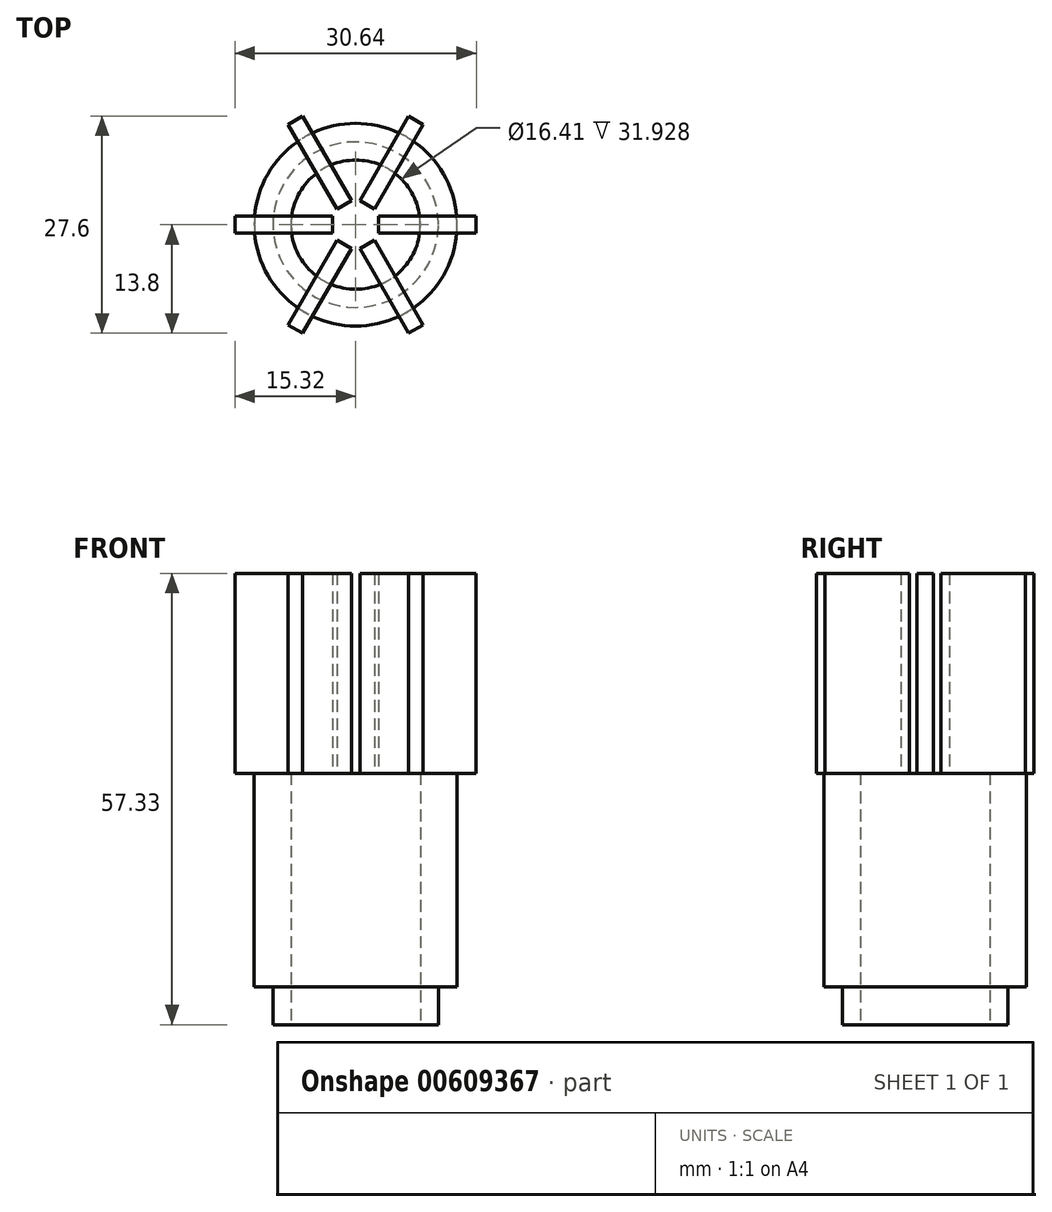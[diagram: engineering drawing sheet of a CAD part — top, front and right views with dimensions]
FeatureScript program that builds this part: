
annotation { "Feature Type Name" : "Feature", "Feature Type Description" : "" }
export const myFeature = defineFeature(function(context is Context, id is Id, definition is map)
    precondition{}
    {
        {
            var Q0;
            Q0=qCreatedBy(makeId("Front.planeOp"),FACE);
            var sketch = newSketch(context, id + "F0", { "sketchPlane" : qUnion([Q0])});
            skLineSegment(sketch, "E0", {"start": v(0, 0) * mm, "end": v(0, 36.56) * mm});
            skSolve(sketch);
        }
        {
            var Q0;
            Q0=qCreatedBy(makeId("Front.planeOp"),FACE);
            var sketch = newSketch(context, id + "F1", { "sketchPlane" : qUnion([Q0])});
            skLineSegment(sketch, "E1", {"start": v(8.2, 0) * mm, "end": v(12.88, 0) * mm});
            skLineSegment(sketch, "E2", {"start": v(12.88, 0) * mm, "end": v(12.88, -1.71) * mm});
            skLineSegment(sketch, "E3", {"start": v(12.88, -1.71) * mm, "end": v(10.5, -1.71) * mm});
            skLineSegment(sketch, "E4", {"start": v(10.5, -1.71) * mm, "end": v(10.5, -6.53) * mm});
            skLineSegment(sketch, "E5", {"start": v(10.5, -6.53) * mm, "end": v(8.2, -6.53) * mm});
            skLineSegment(sketch, "E6", {"start": v(8.2, -6.53) * mm, "end": v(8.2, 0) * mm});
            skSolve(sketch);
        }
        {
            var Q0;
            Q0=makeQuery(id+"F1.imprint","IMPRINT",FACE,{"disambiguationData":[TD([[makeQuery(id+"F1.imprint","IMPRINT",EDGE,{"derivedFrom":sQuery(id+"F1.wireOp",EDGE,"E1")}),-1.0]])]});
            var Q1;
            Q1=sQuery(id+"F0.wireOp",EDGE,"E0");
            revolve(context, id + "F2", {"entities" : qUnion([Q0]), "axis" : qUnion([Q1]), "revolveType" : RevolveType.FULL});
        }
        {
            var Q0;
            Q0=makeQuery(id+"F2.opRevolve","SWEPT_FACE",FACE,{"disambiguationData":[OSD([sQuery(id+"F1.wireOp",EDGE,"E1")])]});
            extrude(context, id + "F3", {"entities" : qUnion([Q0]), "operationType" : NewBodyOperationType.ADD, "depth" : 25.4 * mm, "offsetDistance" : 25.4 * mm});
        }
        {
            var Q0;
            Q0=makeQuery(id+"F3.opExtrude","CAP_FACE",FACE,{"disambiguationData":[OSD([sQuery(id+"F1.wireOp",EDGE,"E1")])],"isStart":false});
            var sketch = newSketch(context, id + "F4", { "sketchPlane" : qUnion([Q0])});
            skLineSegment(sketch, "E7.bottom", {"start": v(2.9, 1.07) * mm, "end": v(15.32, 1.07) * mm});
            skLineSegment(sketch, "E7.top", {"start": v(2.9, -1.07) * mm, "end": v(15.32, -1.07) * mm});
            skLineSegment(sketch, "E7.left", {"start": v(2.9, 1.07) * mm, "end": v(2.9, -1.07) * mm});
            skLineSegment(sketch, "E7.right", {"start": v(15.32, 1.07) * mm, "end": v(15.32, -1.07) * mm});
            skPoint(sketch, "E8", {"position": v(2.9, 0) * mm});
            skPoint(sketch, "E9.1.0", {"position": v(1.45, 2.52) * mm});
            skLineSegment(sketch, "E9.1.1", {"start": v(0.53, 3.05) * mm, "end": v(6.73, 13.8) * mm});
            skLineSegment(sketch, "E9.1.2", {"start": v(2.38, 1.99) * mm, "end": v(8.58, 12.73) * mm});
            skLineSegment(sketch, "E9.1.3", {"start": v(6.73, 13.8) * mm, "end": v(8.58, 12.73) * mm});
            skLineSegment(sketch, "E9.1.4", {"start": v(0.53, 3.05) * mm, "end": v(2.38, 1.99) * mm});
            skPoint(sketch, "E9.2.0", {"position": v(-1.45, 2.52) * mm});
            skLineSegment(sketch, "E9.2.1", {"start": v(-2.38, 1.99) * mm, "end": v(-8.58, 12.73) * mm});
            skLineSegment(sketch, "E9.2.2", {"start": v(-0.53, 3.05) * mm, "end": v(-6.73, 13.8) * mm});
            skLineSegment(sketch, "E9.2.3", {"start": v(-8.58, 12.73) * mm, "end": v(-6.73, 13.8) * mm});
            skLineSegment(sketch, "E9.2.4", {"start": v(-2.38, 1.99) * mm, "end": v(-0.53, 3.05) * mm});
            skPoint(sketch, "E9.3.0", {"position": v(-2.9, 0) * mm});
            skLineSegment(sketch, "E9.3.1", {"start": v(-2.9, -1.07) * mm, "end": v(-15.32, -1.07) * mm});
            skLineSegment(sketch, "E9.3.2", {"start": v(-2.9, 1.07) * mm, "end": v(-15.32, 1.07) * mm});
            skLineSegment(sketch, "E9.3.3", {"start": v(-15.32, -1.07) * mm, "end": v(-15.32, 1.07) * mm});
            skLineSegment(sketch, "E9.3.4", {"start": v(-2.9, -1.07) * mm, "end": v(-2.9, 1.07) * mm});
            skPoint(sketch, "E9.4.0", {"position": v(-1.45, -2.52) * mm});
            skLineSegment(sketch, "E9.4.1", {"start": v(-0.53, -3.05) * mm, "end": v(-6.73, -13.8) * mm});
            skLineSegment(sketch, "E9.4.2", {"start": v(-2.38, -1.99) * mm, "end": v(-8.58, -12.73) * mm});
            skLineSegment(sketch, "E9.4.3", {"start": v(-6.73, -13.8) * mm, "end": v(-8.58, -12.73) * mm});
            skLineSegment(sketch, "E9.4.4", {"start": v(-0.53, -3.05) * mm, "end": v(-2.38, -1.99) * mm});
            skPoint(sketch, "E9.5.0", {"position": v(1.45, -2.52) * mm});
            skLineSegment(sketch, "E9.5.1", {"start": v(2.38, -1.99) * mm, "end": v(8.58, -12.73) * mm});
            skLineSegment(sketch, "E9.5.2", {"start": v(0.53, -3.05) * mm, "end": v(6.73, -13.8) * mm});
            skLineSegment(sketch, "E9.5.3", {"start": v(8.58, -12.73) * mm, "end": v(6.73, -13.8) * mm});
            skLineSegment(sketch, "E9.5.4", {"start": v(2.38, -1.99) * mm, "end": v(0.53, -3.05) * mm});
            skPoint(sketch, "E9.center", {"position": v(0, 0) * mm});
            skSolve(sketch);
        }
        {
            var Q0;
            Q0 = qSketchRegion(id + "F4", true);
            extrude(context, id + "F5", {"entities" : qUnion([Q0]), "operationType" : NewBodyOperationType.ADD, "depth" : 25.4 * mm, "offsetDistance" : 25.4 * mm});
        }
    });
